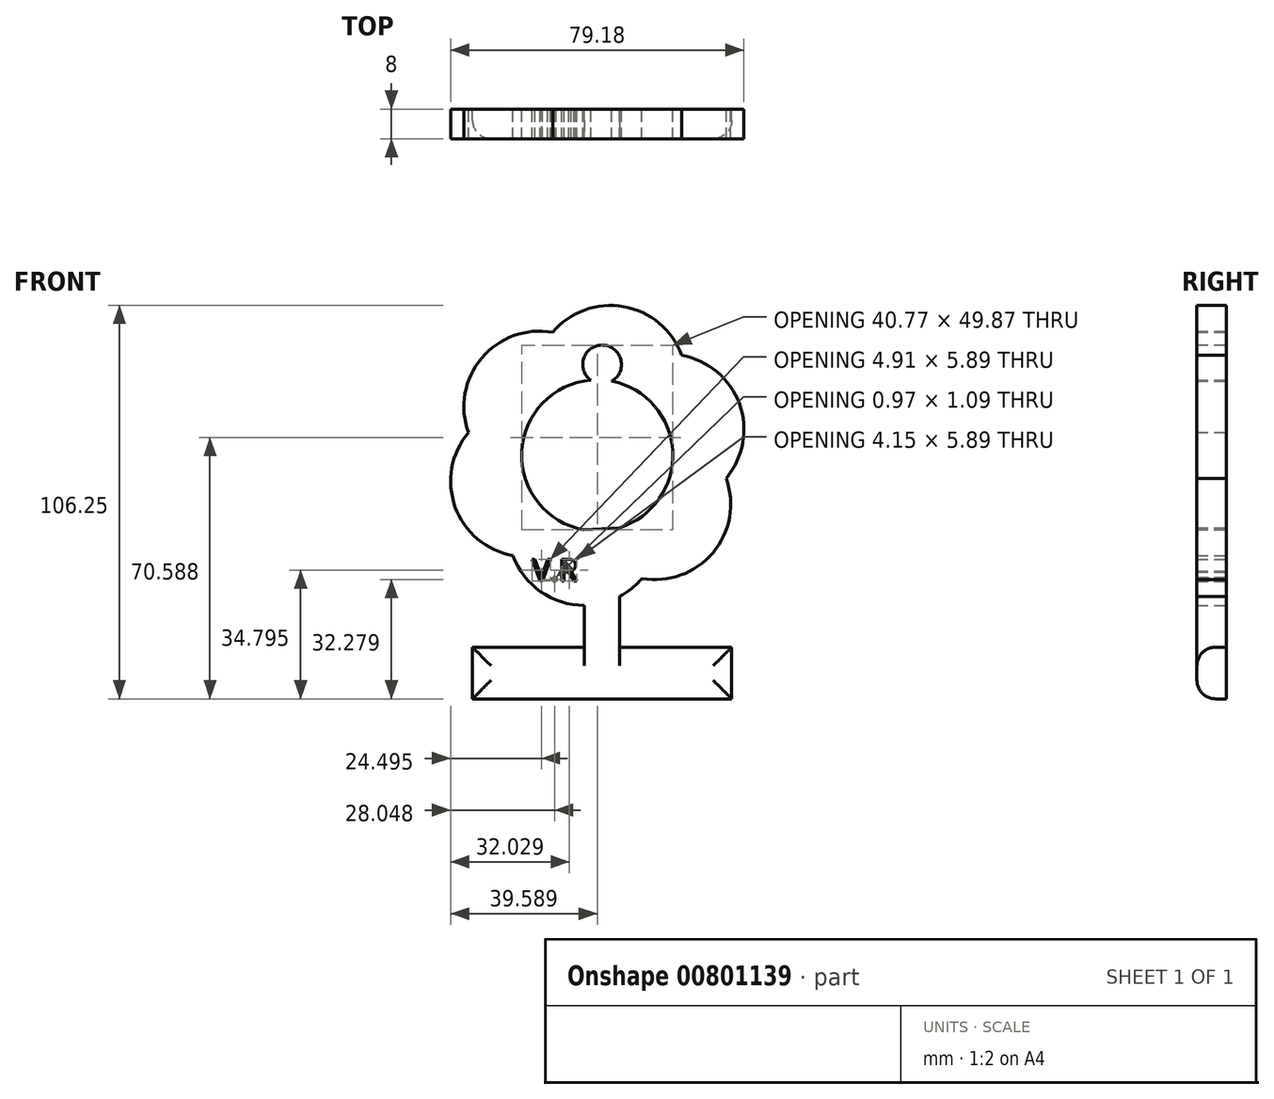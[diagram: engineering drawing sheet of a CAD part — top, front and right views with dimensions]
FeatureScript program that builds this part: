
annotation { "Feature Type Name" : "Feature", "Feature Type Description" : "" }
export const myFeature = defineFeature(function(context is Context, id is Id, definition is map)
    precondition{}
    {
        {
            var Q0;
            Q0=qCreatedBy(makeId("Front.planeOp"),FACE);
            var sketch = newSketch(context, id + "F0", { "sketchPlane" : qUnion([Q0])});
            skLineSegment(sketch, "E0.bottom", {"start": v(-35, 6.97) * mm, "end": v(35, 6.97) * mm});
            skLineSegment(sketch, "E0.top", {"start": v(-35, -6.98) * mm, "end": v(35, -6.98) * mm});
            skLineSegment(sketch, "E0.left", {"start": v(-35, 6.97) * mm, "end": v(-35, -6.98) * mm});
            skLineSegment(sketch, "E0.right", {"start": v(35, 6.97) * mm, "end": v(35, -6.98) * mm});
            skPoint(sketch, "E0.middle", {"position": v(0, 0) * mm});
            skLineSegment(sketch, "E1.bottom", {"start": v(-4.86, 38.67) * mm, "end": v(4.68, 39.26) * mm});
            skLineSegment(sketch, "E1.left", {"start": v(-4.86, 38.67) * mm, "end": v(-4.76, -6.98) * mm});
            skLineSegment(sketch, "E1.right", {"start": v(4.68, 39.26) * mm, "end": v(4.79, -6.98) * mm});
            skPoint(sketch, "E1.top.end.orphan", {"position": v(4.86, -38.67) * mm});
            skPoint(sketch, "E1.top.start.orphan", {"position": v(-4.68, -39.26) * mm});
            skArc(sketch, "E2", {"start": v(4.68, 39.26) * mm, "mid": v(-2.54, 79.14) * mm, "end": v(-4.86, 38.67) * mm});
            skArc(sketch, "E3", {"start": v(-1.3, 58.77) * mm, "mid": v(-40.57, 55.38) * mm, "end": v(-4.86, 38.67) * mm});
            skArc(sketch, "E4", {"start": v(-1.3, 58.77) * mm, "mid": v(-23.87, 91.09) * mm, "end": v(-20.48, 51.81) * mm});
            skArc(sketch, "E5", {"start": v(-1.3, 58.77) * mm, "mid": v(15.4, 94.48) * mm, "end": v(-16.91, 71.9) * mm});
            skArc(sketch, "E6", {"start": v(-1.3, 58.77) * mm, "mid": v(37.98, 62.16) * mm, "end": v(2.27, 78.86) * mm});
            skArc(sketch, "E7", {"start": v(-1.3, 58.77) * mm, "mid": v(-5.77, 49.2) * mm, "end": v(-4.86, 38.67) * mm});
            skArc(sketch, "E8", {"start": v(-1.3, 58.77) * mm, "mid": v(-18, 23.06) * mm, "end": v(14.32, 45.63) * mm});
            skArc(sketch, "E9.trimOffspring", {"start": v(4.7, 27.63) * mm, "mid": v(33.6, 38.96) * mm, "end": v(17.89, 65.72) * mm});
            skCircle(sketch, "E10", {"center": v(0, 83.32) * mm, "radius": 5.23 * mm});
            skText(sketch, "E11", { "text": "V.R", "fontName": "OpenSans-Regular.ttf"});
            const initialGuessF0  = {"E11": [-0.01885, 0.02487, 1, 0, 0.00594]};
            skSetInitialGuess(sketch, initialGuessF0);
            skSolve(sketch);
        }
        {
            var Q0;
            Q0 = qSketchRegion(id + "F0", true);
            extrude(context, id + "F1", {"entities" : qUnion([Q0]), "depth" : 8 * mm, "offsetDistance" : 25 * mm});
        }
        {
            var Q0;
            {var subQ0=sQuery(id+"F0.wireOp",EDGE,"E0.bottom");Q0=makeQuery(id+"F1.opExtrude","CAP_EDGE",EDGE,{"disambiguationData":[OSD([subQ0]),TDD([makeQuery(id+"F0.imprint","IMPRINT",EDGE,{"disambiguationData":[TD([[makeQuery(id+"F0.imprint","INTERSECT",VERTEX,{"derivedFrom":[subQ0,sQuery(id+"F0.wireOp",EDGE,"E0.left")]}),-1.0]])],"derivedFrom":subQ0})])],"isStart":false});}
            var Q1;
            Q1=makeQuery(id+"F1.opExtrude","CAP_EDGE",EDGE,{"disambiguationData":[OSD([sQuery(id+"F0.wireOp",EDGE,"E0.left")])],"isStart":false});
            var Q2;
            Q2=makeQuery(id+"F1.opExtrude","CAP_EDGE",EDGE,{"disambiguationData":[OSD([sQuery(id+"F0.wireOp",EDGE,"E0.top")])],"isStart":false});
            var Q3;
            Q3=makeQuery(id+"F1.opExtrude","CAP_EDGE",EDGE,{"disambiguationData":[OSD([sQuery(id+"F0.wireOp",EDGE,"E0.right")])],"isStart":false});
            var Q4;
            {var subQ0=sQuery(id+"F0.wireOp",EDGE,"E0.bottom");Q4=makeQuery(id+"F1.opExtrude","CAP_EDGE",EDGE,{"disambiguationData":[OSD([subQ0]),TDD([makeQuery(id+"F0.imprint","IMPRINT",EDGE,{"disambiguationData":[TD([[makeQuery(id+"F0.imprint","INTERSECT",VERTEX,{"derivedFrom":[subQ0,sQuery(id+"F0.wireOp",EDGE,"E0.right")]}),1.0]])],"derivedFrom":subQ0})])],"isStart":false});}
            fillet(context, id + "F2", {"entities" : qUnion([Q0, Q1, Q2, Q3, Q4]), "radius" : 5 * mm, "tangentPropagation" : true, "allowEdgeOverflow" : false});
        }
    });
